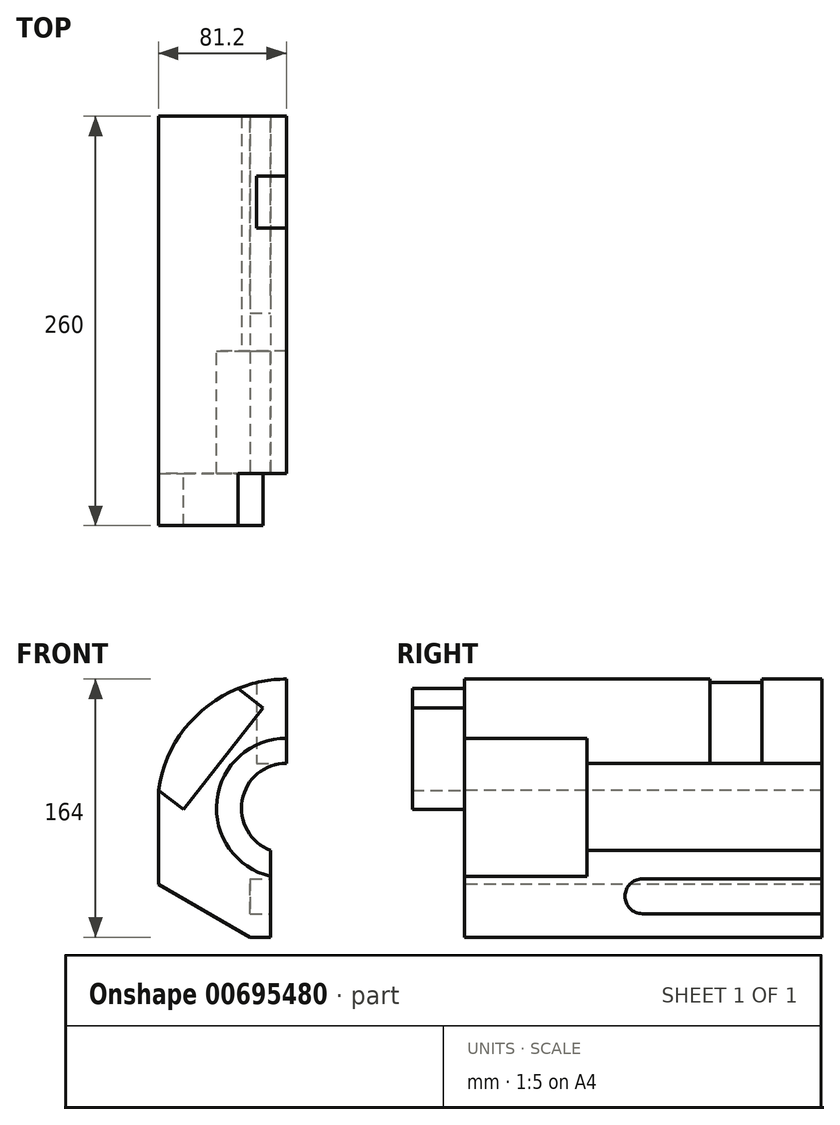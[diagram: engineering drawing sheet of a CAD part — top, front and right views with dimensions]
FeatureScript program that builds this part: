
annotation { "Feature Type Name" : "Feature", "Feature Type Description" : "" }
export const myFeature = defineFeature(function(context is Context, id is Id, definition is map)
    precondition{}
    {
        {
            var Q0;
            Q0=qCreatedBy(makeId("Front.planeOp"),FACE);
            var sketch = newSketch(context, id + "F0", { "sketchPlane" : qUnion([Q0])});
            skArc(sketch, "E0", {"start": v(0, 82) * mm, "mid": v(-53.8, 61.89) * mm, "end": v(-81.2, 11.41) * mm});
            skLineSegment(sketch, "E1", {"start": v(-10, -82) * mm, "end": v(-23, -82) * mm});
            skLineSegment(sketch, "E2", {"start": v(-10, -82) * mm, "end": v(-10, -26.77) * mm});
            skPoint(sketch, "E3", {"position": v(-23, -82) * mm});
            skLineSegment(sketch, "E4", {"start": v(-23, -82) * mm, "end": v(-81.2, -48.4) * mm});
            skLineSegment(sketch, "E5", {"start": v(0, 0) * mm, "end": v(-64.62, 50.48) * mm, "construction": true});
            skPoint(sketch, "E6", {"position": v(-81.2, 11.41) * mm});
            skPoint(sketch, "E7", {"position": v(-30.72, 76.03) * mm});
            skLineSegment(sketch, "E8", {"start": v(-81.2, 11.41) * mm, "end": v(-81.2, -48.4) * mm});
            skLineSegment(sketch, "E9", {"start": v(0, 82) * mm, "end": v(0, 28.58) * mm});
            skArc(sketch, "E10", {"start": v(0, 28.57) * mm, "mid": v(-28.12, 5.08) * mm, "end": v(-10, -26.77) * mm});
            skPoint(sketch, "E11.orphan", {"position": v(-10, 0) * mm});
            skPoint(sketch, "E12.orphan", {"position": v(0, -82) * mm});
            skSolve(sketch);
        }
        {
            var Q0;
            Q0=makeQuery(id+"F0.imprint","IMPRINT",FACE,{"disambiguationData":[TD([[makeQuery(id+"F0.imprint","IMPRINT",EDGE,{"derivedFrom":sQuery(id+"F0.wireOp",EDGE,"E0")}),1.0]])]});
            extrude(context, id + "F1", {"entities" : qUnion([Q0]), "oppositeDirection" : true, "depth" : 227 * mm, "offsetDistance" : 25 * mm});
        }
        {
            var Q0;
            Q0=makeQuery(id+"F1.opExtrude","CAP_FACE",FACE,{"disambiguationData":[OSD([sQuery(id+"F0.wireOp",EDGE,"E0"),sQuery(id+"F0.wireOp",EDGE,"E1"),sQuery(id+"F0.wireOp",EDGE,"E2"),sQuery(id+"F0.wireOp",EDGE,"E4"),sQuery(id+"F0.wireOp",EDGE,"E8"),sQuery(id+"F0.wireOp",EDGE,"E9"),sQuery(id+"F0.wireOp",EDGE,"E10")])],"isStart":true});
            cPlane(context, id + "F2", {"entities" : qUnion([Q0]), "cplaneType" : CPlaneType.OFFSET, "offset" : 78 * mm, "oppositeDirection" : true, "width" : 150 * mm, "height" : 150 * mm});
        }
        {
            var Q0;
            Q0=qCreatedBy(id+"F2.planeOp",FACE);
            var sketch = newSketch(context, id + "F3", { "sketchPlane" : qUnion([Q0])});
            skCircle(sketch, "E13", {"center": v(0, 0) * mm, "radius": 44.45 * mm});
            skSolve(sketch);
        }
        {
            var Q0;
            Q0=makeQuery(id+"F3.imprint","IMPRINT",FACE,{"disambiguationData":[TD([[makeQuery(id+"F3.imprint","IMPRINT",EDGE,{"derivedFrom":sQuery(id+"F3.wireOp",EDGE,"E13")}),1.0]])]});
            extrude(context, id + "F4", {"entities" : qUnion([Q0]), "operationType" : NewBodyOperationType.REMOVE, "endBound" : BoundingType.THROUGH_ALL, "depth" : 25 * mm, "offsetDistance" : 25 * mm});
        }
        {
            var Q0;
            Q0=makeQuery(id+"F0.imprint","IMPRINT",FACE,{"disambiguationData":[TD([[makeQuery(id+"F0.imprint","IMPRINT",EDGE,{"derivedFrom":sQuery(id+"F0.wireOp",EDGE,"E0")}),1.0]])]});
            var sketch = newSketch(context, id + "F5", { "sketchPlane" : qUnion([Q0])});
            skPoint(sketch, "E14.0", {"position": v(-30.72, 76.03) * mm});
            skPoint(sketch, "E15.0", {"position": v(-81.2, 11.41) * mm});
            skPoint(sketch, "E16.0", {"position": v(-64.62, 50.48) * mm});
            skLineSegment(sketch, "E17", {"start": v(-30.72, 76.03) * mm, "end": v(-14.95, 63.7) * mm});
            skLineSegment(sketch, "E18", {"start": v(-81.2, 11.41) * mm, "end": v(-65.43, -0.9) * mm});
            skLineSegment(sketch, "E19", {"start": v(-65.43, -0.9) * mm, "end": v(-14.95, 63.7) * mm});
            skArc(sketch, "E20", {"start": v(-30.72, 76.03) * mm, "mid": v(-64.62, 50.48) * mm, "end": v(-81.2, 11.41) * mm});
            skSolve(sketch);
        }
        {
            var Q0;
            Q0=makeQuery(id+"F5.imprint","IMPRINT",FACE,{"disambiguationData":[TD([[makeQuery(id+"F5.imprint","IMPRINT",EDGE,{"derivedFrom":sQuery(id+"F5.wireOp",EDGE,"E17")}),-1.0]])]});
            extrude(context, id + "F6", {"entities" : qUnion([Q0]), "operationType" : NewBodyOperationType.ADD, "depth" : 33 * mm, "offsetDistance" : 25 * mm});
        }
        {
            var Q0;
            Q0=makeQuery(id+"F1.opExtrude","SWEPT_FACE",FACE,{"disambiguationData":[OSD([sQuery(id+"F0.wireOp",EDGE,"E9")])]});
            var sketch = newSketch(context, id + "F7", { "sketchPlane" : qUnion([Q0])});
            skLineSegment(sketch, "E21.0", {"start": v(227, 82) * mm, "end": v(0, 82) * mm});
            skLineSegment(sketch, "E22.0", {"start": v(227, 28.57) * mm, "end": v(78, 28.57) * mm});
            skLineSegment(sketch, "E23", {"start": v(189, 82) * mm, "end": v(189, 28.58) * mm});
            skLineSegment(sketch, "E24", {"start": v(189, 28.57) * mm, "end": v(156, 28.57) * mm});
            skLineSegment(sketch, "E25", {"start": v(156, 28.57) * mm, "end": v(156, 82) * mm});
            skLineSegment(sketch, "E26", {"start": v(156, 82) * mm, "end": v(189, 82) * mm});
            skSolve(sketch);
        }
        {
            var Q0;
            {var subQ0=sQuery(id+"F7.wireOp",EDGE,"E23");Q0=makeQuery(id+"F7.imprint","IMPRINT",FACE,{"disambiguationData":[TD([[makeQuery(id+"F7.imprint","IMPRINT",EDGE,{"derivedFrom":subQ0}),-1.0]])]});}
            extrude(context, id + "F8", {"entities" : qUnion([Q0]), "operationType" : NewBodyOperationType.REMOVE, "oppositeDirection" : true, "depth" : 19 * mm, "offsetDistance" : 25 * mm});
        }
        {
            var Q0;
            Q0=makeQuery(id+"F1.opExtrude","SWEPT_FACE",FACE,{"disambiguationData":[OSD([sQuery(id+"F0.wireOp",EDGE,"E2")])]});
            var sketch = newSketch(context, id + "F9", { "sketchPlane" : qUnion([Q0])});
            skPoint(sketch, "E27.0", {"position": v(227, -82) * mm});
            skLineSegment(sketch, "E28", {"start": v(227, -56) * mm, "end": v(113, -56) * mm, "construction": true});
            skArc(sketch, "E29", {"start": v(113, -45) * mm, "mid": v(102, -56) * mm, "end": v(113, -67) * mm});
            skLineSegment(sketch, "E30", {"start": v(113, -45) * mm, "end": v(227, -45) * mm});
            skLineSegment(sketch, "E31", {"start": v(227, -45) * mm, "end": v(227, -67) * mm});
            skLineSegment(sketch, "E32", {"start": v(227, -67) * mm, "end": v(113, -67) * mm});
            skSolve(sketch);
        }
        {
            var Q0;
            Q0=makeQuery(id+"F9.imprint","IMPRINT",FACE,{"disambiguationData":[TD([[makeQuery(id+"F9.imprint","IMPRINT",EDGE,{"derivedFrom":sQuery(id+"F9.wireOp",EDGE,"E29")}),1.0]])]});
            extrude(context, id + "F10", {"entities" : qUnion([Q0]), "operationType" : NewBodyOperationType.REMOVE, "oppositeDirection" : true, "depth" : 13 * mm, "offsetDistance" : 25 * mm});
        }
    });
